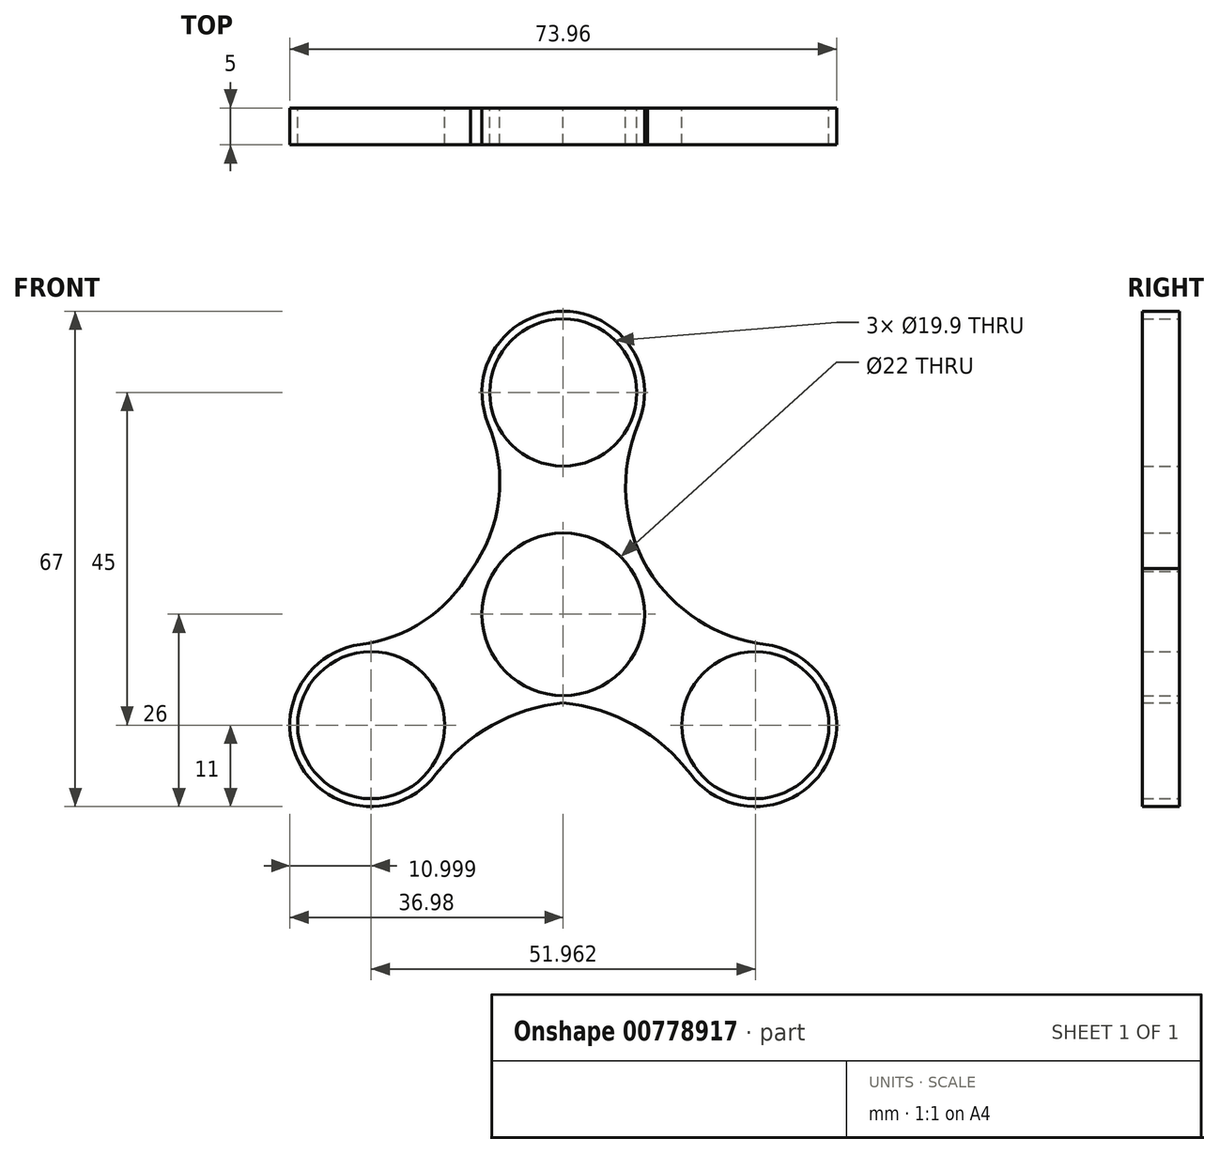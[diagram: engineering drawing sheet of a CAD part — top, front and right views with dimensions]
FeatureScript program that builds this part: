
annotation { "Feature Type Name" : "Feature", "Feature Type Description" : "" }
export const myFeature = defineFeature(function(context is Context, id is Id, definition is map)
    precondition{}
    {
        {
            var Q0;
            Q0=qCreatedBy(makeId("Front.planeOp"),FACE);
            var sketch = newSketch(context, id + "F0", { "sketchPlane" : qUnion([Q0])});
            skCircle(sketch, "E0", {"center": v(0, 30) * mm, "radius": 9.95 * mm});
            skArc(sketch, "E1", {"start": v(10.14, 25.74) * mm, "mid": v(-0.02, 41) * mm, "end": v(-10.13, 25.7) * mm});
            skArc(sketch, "E2", {"start": v(10.58, 26.71) * mm, "mid": v(8.44, 16.34) * mm, "end": v(11.4, 6.17) * mm});
            skArc(sketch, "E3.MirrorCS", {"start": v(-10.58, 26.71) * mm, "mid": v(-8.66, 16) * mm, "end": v(-12.55, 5.83) * mm});
            skPoint(sketch, "E4.orphan", {"position": v(12.15, 4.98) * mm});
            skPoint(sketch, "E5.orphan", {"position": v(-12.73, 5.6) * mm});
            skArc(sketch, "E6.1.0", {"start": v(-27.33, -4.08) * mm, "mid": v(-35.5, -20.5) * mm, "end": v(-17.2, -21.62) * mm});
            skCircle(sketch, "E6.1.1", {"center": v(-25.98, -15) * mm, "radius": 9.95 * mm});
            skArc(sketch, "E6.1.2", {"start": v(-17.85, -22.52) * mm, "mid": v(-10.08, -15.28) * mm, "end": v(0, -11.98) * mm});
            skArc(sketch, "E6.1.3", {"start": v(-28.42, -4.2) * mm, "mid": v(-19.24, -1.16) * mm, "end": v(-12.55, 5.83) * mm});
            skArc(sketch, "E6.2.0", {"start": v(17.2, -21.62) * mm, "mid": v(35.5, -20.5) * mm, "end": v(27.33, -4.08) * mm});
            skCircle(sketch, "E6.2.1", {"center": v(25.98, -15) * mm, "radius": 9.95 * mm});
            skArc(sketch, "E6.2.2", {"start": v(28.42, -4.2) * mm, "mid": v(18.68, -1.05) * mm, "end": v(11.4, 6.17) * mm});
            skArc(sketch, "E6.2.3", {"start": v(17.85, -22.52) * mm, "mid": v(10.08, -15.28) * mm, "end": v(0, -11.98) * mm});
            skPoint(sketch, "E6.center", {"position": v(0, 0) * mm});
            skPoint(sketch, "E7.orphan", {"position": v(-12.18, 6.36) * mm});
            skPoint(sketch, "E8.orphan", {"position": v(-11.75, 7.4) * mm});
            skPoint(sketch, "E9.orphan", {"position": v(11.6, 5.82) * mm});
            skPoint(sketch, "E10.orphan", {"position": v(10.83, 7.14) * mm});
            skPoint(sketch, "E11.orphan", {"position": v(-0.87, -11.9) * mm});
            skPoint(sketch, "E12.orphan", {"position": v(0.87, -11.9) * mm});
            skCircle(sketch, "E13", {"center": v(0, 0) * mm, "radius": 11 * mm});
            skSolve(sketch);
        }
        {
            var Q0;
            Q0=makeQuery(id+"F0.imprint","IMPRINT",FACE,{"disambiguationData":[TD([[makeQuery(id+"F0.imprint","IMPRINT",EDGE,{"derivedFrom":sQuery(id+"F0.wireOp",EDGE,"E0")}),-1.0]])]});
            extrude(context, id + "F1", {"entities" : qUnion([Q0]), "depth" : 5 * mm, "offsetDistance" : 25 * mm});
        }
    });
